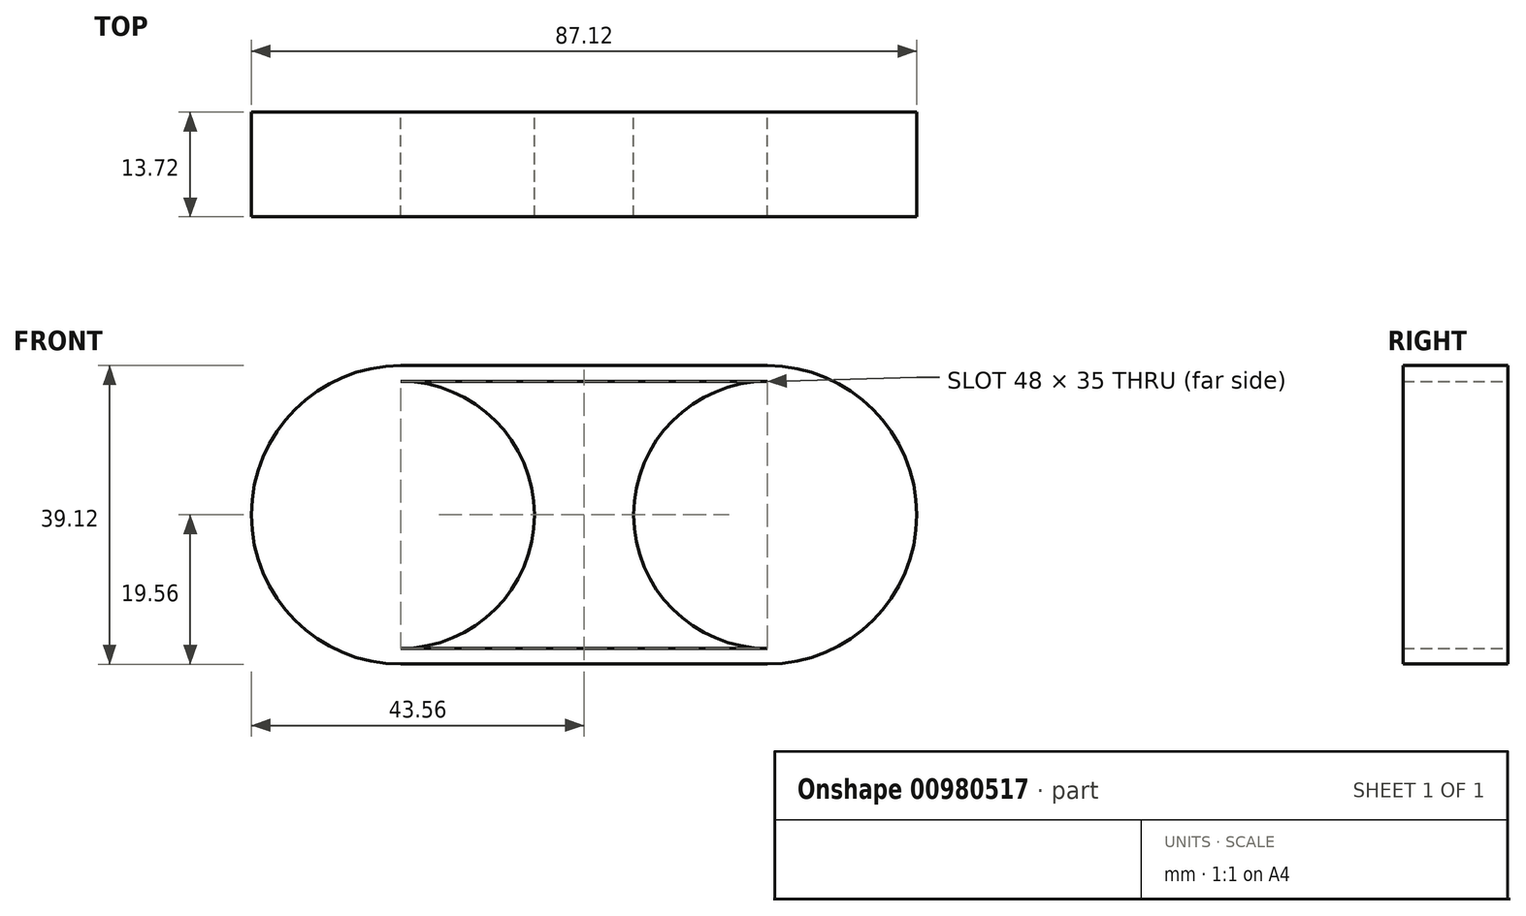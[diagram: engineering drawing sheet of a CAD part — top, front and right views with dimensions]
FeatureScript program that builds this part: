
annotation { "Feature Type Name" : "Feature", "Feature Type Description" : "" }
export const myFeature = defineFeature(function(context is Context, id is Id, definition is map)
    precondition{}
    {
        {
            var Q0;
            Q0=qCreatedBy(makeId("Front.planeOp"),FACE);
            var sketch = newSketch(context, id + "F0", { "sketchPlane" : qUnion([Q0])});
            skCircle(sketch, "E0", {"center": v(0, 0) * mm, "radius": 17.5 * mm});
            skCircle(sketch, "E1", {"center": v(48, 0) * mm, "radius": 17.5 * mm});
            skArc(sketch, "E2", {"start": v(0, 19.56) * mm, "mid": v(-19.56, 0) * mm, "end": v(0, -19.56) * mm});
            skArc(sketch, "E3", {"start": v(48, -19.56) * mm, "mid": v(67.56, 0) * mm, "end": v(48, 19.56) * mm});
            skLineSegment(sketch, "E4", {"start": v(0, 19.56) * mm, "end": v(48, 19.56) * mm});
            skLineSegment(sketch, "E5", {"start": v(0, -19.56) * mm, "end": v(48, -19.56) * mm});
            skLineSegment(sketch, "E6", {"start": v(0, -17.5) * mm, "end": v(48, -17.5) * mm});
            skLineSegment(sketch, "E7", {"start": v(0, 17.5) * mm, "end": v(48, 17.5) * mm});
            skSolve(sketch);
        }
        {
            var Q0;
            Q0=makeQuery(id+"F0.imprint","IMPRINT",FACE,{"disambiguationData":[TD([[makeQuery(id+"F0.imprint","IMPRINT",EDGE,{"derivedFrom":sQuery(id+"F0.wireOp",EDGE,"E2")}),1.0]])]});
            var Q1;
            {var subQ0=sQuery(id+"F0.wireOp",EDGE,"E0");var subQ1=makeQuery(id+"F0.imprint","INTERSECT",VERTEX,{"derivedFrom":[subQ0,sQuery(id+"F0.wireOp",EDGE,"E6")]});Q1=makeQuery(id+"F0.imprint","IMPRINT",FACE,{"disambiguationData":[TD([[makeQuery(id+"F0.imprint","IMPRINT",EDGE,{"disambiguationData":[TD([[subQ1,1.0]])],"derivedFrom":subQ0}),1.0]])]});}
            var Q2;
            {var subQ0=sQuery(id+"F0.wireOp",EDGE,"E1");var subQ1=makeQuery(id+"F0.imprint","INTERSECT",VERTEX,{"derivedFrom":[subQ0,sQuery(id+"F0.wireOp",EDGE,"E6")]});Q2=makeQuery(id+"F0.imprint","IMPRINT",FACE,{"disambiguationData":[TD([[makeQuery(id+"F0.imprint","IMPRINT",EDGE,{"disambiguationData":[TD([[subQ1,1.0]])],"derivedFrom":subQ0}),1.0]])]});}
            extrude(context, id + "F1", {"entities" : qUnion([Q0, Q1, Q2]), "depth" : 13.72 * mm, "offsetDistance" : 25.4 * mm});
        }
    });
